# Revit family: KB3000-AHL-0001
name_source: partatom
category: Equipement spécialisé
units: mm (PartAtom-declared; Revit-internal decimal feet)

## family parameters
Autoriser la découpe dans les vues = Non
Conserver l'orientation des annotations = Non
Cote de connecteur circulaire = Utiliser le diamètre
Couper avec des vides une fois chargée = Non
Hôte = Face
Numéro OmniClass = 23.40.20.21
Partagée = Oui
Repère de localisation dans la pièce = Non
Titre OmniClass = Toilet and Bath Specialties
Type d'élément = Normal

## types (1)
- KB3000
    Body Material = Metal-Koala_Kare-Stainless_Steel-Powder_Coated
    Code d'assemblage = E2010
    Commentaires du type = Adjustable height changing station shall have cut resistant single piece UHMW PE bed surface, attached to continuous 2" (50mm) 
square powder costed steel frame and integrated adjustable front guard. Front guard will be operable with one hand and lock in the 
up and down positions. Changing station shall have two integrated controls to be electronically height adjustable from 12" (300mm) 
- 41" (1040mm) and will have a fail-safe battery backup to prevent against unit failure during power outage. All moving parts shall be 
concealed or guarded in such way at to protect against pinch points or entrapment. The changing station shall be designed to support 
a load of up to 500lbs, with a changing surface that hammocks to provide optimal comfort to the occupant. Bed surface shall be cut 
resistant and field replaceable, with tamper resistant fasteners to connect it to the steel frame. Changing surface shall be no less than 75 
¼" (1911mm) x 31 ½" (800mm). Changing station shall be tested to meet IK10 Rating and shall have no exposed wiring/cables. Changing 
station shall be designed so that it can be hosed down for cleaning and can be used in wet room environment without compromising 
electronics
    Description = Adjustable Height Changing Station
    Elévation par défaut = 0"
    Fabricant = Koala Kare
    Height = 60 15/32"
    Installation Type = Wall Mounted
    Length = 75 5/16"
    Modèle = KB3000
    Nom du vendeur / Seller's name = ANOX Diffusion
    Price = Prices may vary. Please consult Manufacturer Representative for most up-to-date price list.
    Product Page URL = https://www.anox.fr
    URL = https://www.anox.fr
    Width = 40 9/32"

## geometry (parser evidence)
native form markers: Sweep x2
no freeform markers — native parametric forms only
